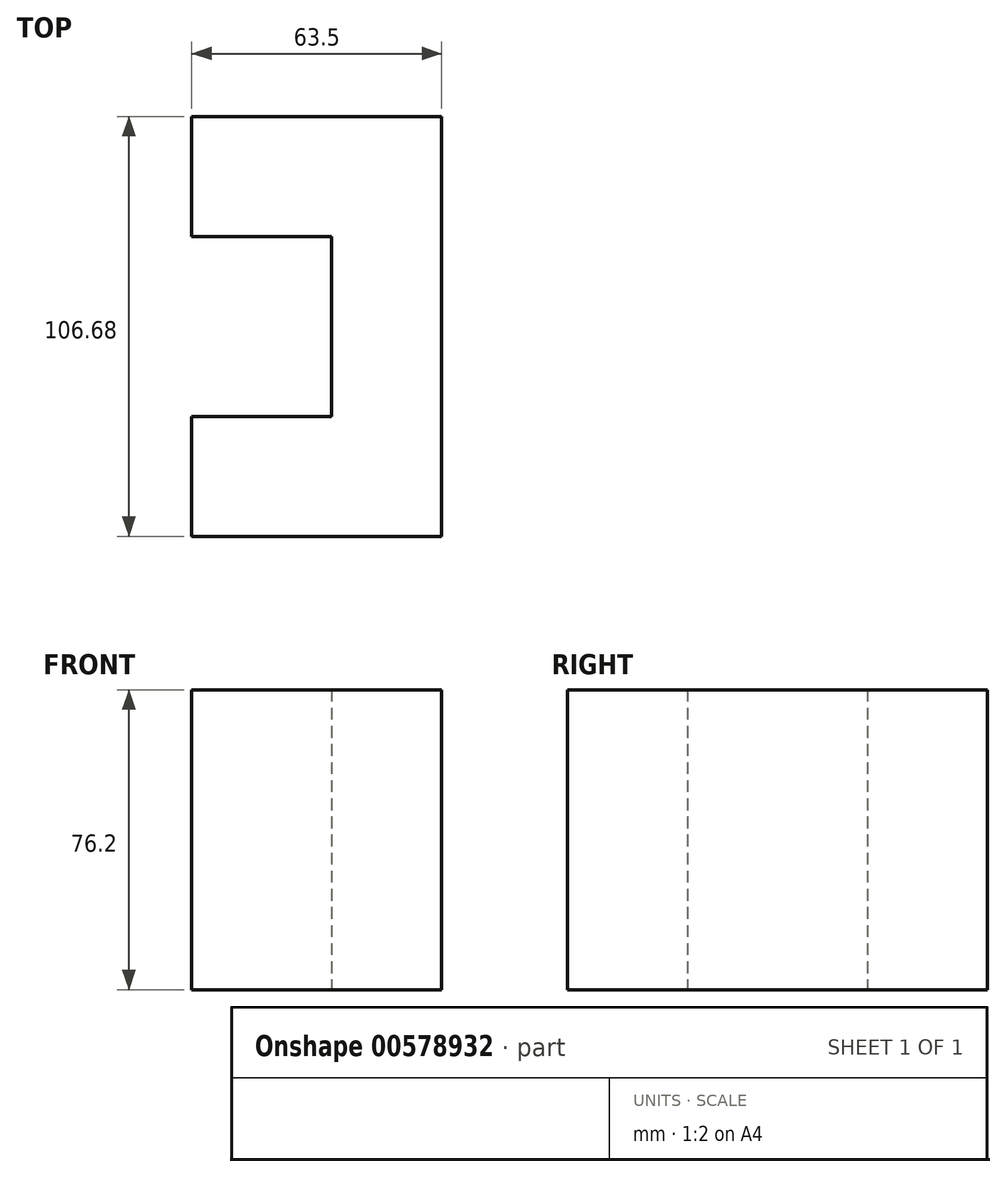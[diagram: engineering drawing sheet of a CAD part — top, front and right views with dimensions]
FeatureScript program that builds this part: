
annotation { "Feature Type Name" : "Feature", "Feature Type Description" : "" }
export const myFeature = defineFeature(function(context is Context, id is Id, definition is map)
    precondition{}
    {
        {
            var Q0;
            Q0=qCreatedBy(makeId("Top.planeOp"),FACE);
            var sketch = newSketch(context, id + "F0", { "sketchPlane" : qUnion([Q0])});
            skLineSegment(sketch, "E0", {"start": v(-30.48, 35.56) * mm, "end": v(33.02, 35.56) * mm});
            skLineSegment(sketch, "E1", {"start": v(33.02, 35.56) * mm, "end": v(33.02, -71.12) * mm});
            skLineSegment(sketch, "E2", {"start": v(33.02, -71.12) * mm, "end": v(-30.48, -71.12) * mm});
            skLineSegment(sketch, "E3", {"start": v(-30.48, -71.12) * mm, "end": v(-30.48, -40.64) * mm});
            skLineSegment(sketch, "E4", {"start": v(-30.48, -40.64) * mm, "end": v(5.08, -40.64) * mm});
            skLineSegment(sketch, "E5", {"start": v(5.08, -40.64) * mm, "end": v(5.08, 5.08) * mm});
            skLineSegment(sketch, "E6", {"start": v(5.08, 5.08) * mm, "end": v(-30.48, 5.08) * mm});
            skLineSegment(sketch, "E7", {"start": v(-30.48, 5.08) * mm, "end": v(-30.48, 35.56) * mm});
            skSolve(sketch);
        }
        {
            var Q0;
            Q0=makeQuery(id+"F0.imprint","IMPRINT",FACE,{"disambiguationData":[TD([[makeQuery(id+"F0.imprint","IMPRINT",EDGE,{"derivedFrom":sQuery(id+"F0.wireOp",EDGE,"E0")}),-1.0]])]});
            extrude(context, id + "F1", {"entities" : qUnion([Q0]), "depth" : 76.2 * mm, "offsetDistance" : 25.4 * mm});
        }
    });
